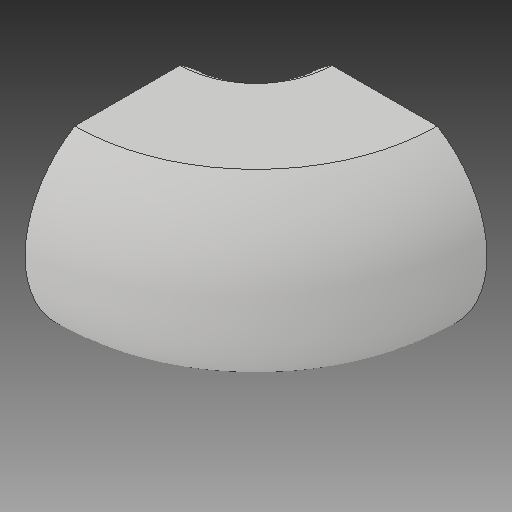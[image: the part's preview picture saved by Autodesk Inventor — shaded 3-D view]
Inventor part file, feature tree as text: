
AUTODESK INVENTOR PART (.ipt)
format: ipt  version: 2017 (Build 210142000, 142)  size: 136,704 bytes
history: native  units: in
note: dims shown in document units (in); Inventor stores cm internally (conversion verified against a paired STEP export)
features: other x1, delete_face x1, sketch x1
ambient origin geometry x8: Origin, YZ Plane, XZ Plane, XY Plane, X Axis, Y Axis, Z Axis, Center Point
bodies: Solid1 (feature_tree)
feature tree (3):
  other  "corridor"
  delete_face  "Delete Face2"
  sketch  "Sketch1"  dims[d1=4.0in d2=90.0deg d28=45.0deg d31=3.8873in]
